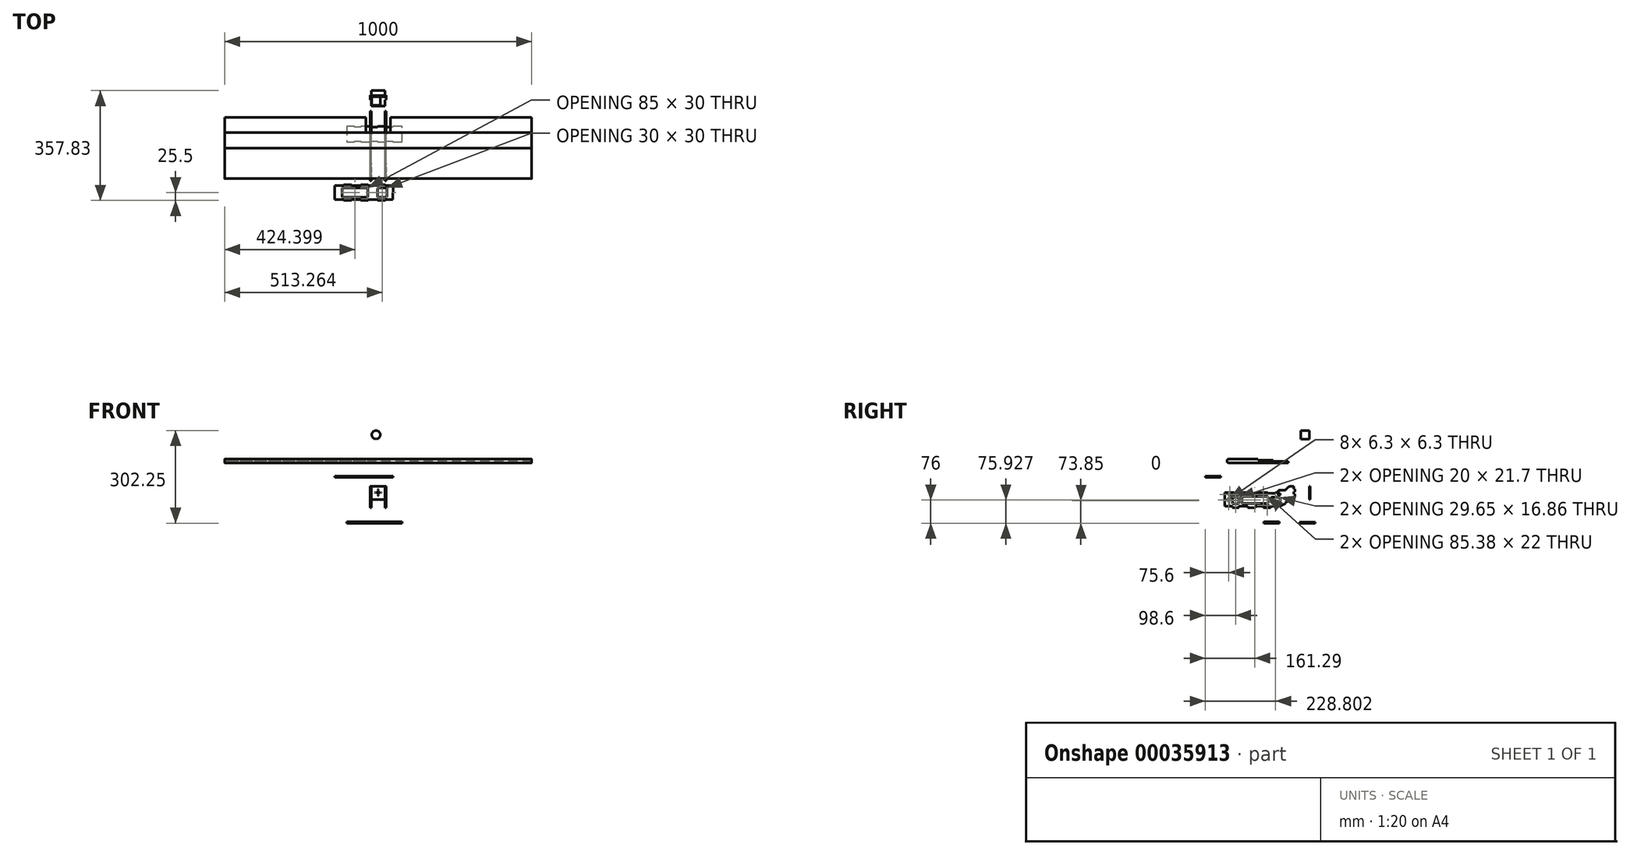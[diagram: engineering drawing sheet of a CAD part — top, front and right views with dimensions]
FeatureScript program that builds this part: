
annotation { "Feature Type Name" : "Feature", "Feature Type Description" : "" }
export const myFeature = defineFeature(function(context is Context, id is Id, definition is map)
    precondition{}
    {
        {
            var Q0;
            Q0=qCreatedBy(makeId("Right.planeOp"),FACE);
            cPlane(context, id + "F0", {"entities" : qUnion([Q0]), "cplaneType" : CPlaneType.OFFSET, "offset" : 22.5 * mm, "width" : 152.4 * mm, "height" : 152.4 * mm});
        }
        {
            var Q0;
            Q0=qCreatedBy(id+"F0.planeOp",FACE);
            var sketch = newSketch(context, id + "F1", { "sketchPlane" : qUnion([Q0])});
            skLineSegment(sketch, "E0", {"start": v(-125, 0) * mm, "end": v(-95, 0) * mm});
            skLineSegment(sketch, "E1", {"start": v(-125, -45) * mm, "end": v(-125, 0) * mm});
            skLineSegment(sketch, "E2", {"start": v(-95, 0) * mm, "end": v(-95, -3) * mm});
            skLineSegment(sketch, "E3", {"start": v(-95, -3) * mm, "end": v(-70, -3) * mm});
            skLineSegment(sketch, "E4", {"start": v(-70, -3) * mm, "end": v(-70, 0) * mm});
            skLineSegment(sketch, "E5", {"start": v(-40, 0) * mm, "end": v(-40, -3) * mm});
            skLineSegment(sketch, "E6", {"start": v(-40, -3) * mm, "end": v(-15, -3) * mm});
            skLineSegment(sketch, "E7", {"start": v(-15, -3) * mm, "end": v(-15, 0) * mm});
            skLineSegment(sketch, "E8", {"start": v(15, 0) * mm, "end": v(15, -3) * mm});
            skLineSegment(sketch, "E9", {"start": v(15, -3) * mm, "end": v(40, -3) * mm});
            skLineSegment(sketch, "E10", {"start": v(40, -3) * mm, "end": v(40, 0) * mm});
            skLineSegment(sketch, "E11", {"start": v(-70, 0) * mm, "end": v(-40, 0) * mm});
            skLineSegment(sketch, "E12", {"start": v(103, 11.5) * mm, "end": v(103, 3) * mm});
            skLineSegment(sketch, "E13", {"start": v(100, -22.5) * mm, "end": v(100, -14) * mm});
            skLineSegment(sketch, "E14", {"start": v(100, -14) * mm, "end": v(103, -14) * mm});
            skLineSegment(sketch, "E15", {"start": v(103, -14) * mm, "end": v(103, -5.5) * mm});
            skLineSegment(sketch, "E16", {"start": v(-125, -45) * mm, "end": v(-100, -45) * mm});
            skLineSegment(sketch, "E17", {"start": v(-100, -49.7) * mm, "end": v(-100, -45) * mm});
            skLineSegment(sketch, "E18", {"start": v(-100, -49.7) * mm, "end": v(-80, -49.7) * mm});
            skLineSegment(sketch, "E19", {"start": v(-80, -45) * mm, "end": v(-80, -49.7) * mm});
            skLineSegment(sketch, "E20", {"start": v(-80, -45) * mm, "end": v(-50, -45) * mm});
            skLineSegment(sketch, "E21", {"start": v(-50, -49.7) * mm, "end": v(-50, -45) * mm});
            skLineSegment(sketch, "E22", {"start": v(-50, -49.7) * mm, "end": v(-25, -49.7) * mm});
            skLineSegment(sketch, "E23", {"start": v(-25, -45) * mm, "end": v(-25, -49.7) * mm});
            skLineSegment(sketch, "E24", {"start": v(-25, -45) * mm, "end": v(0, -45) * mm});
            skLineSegment(sketch, "E25", {"start": v(0, -49.7) * mm, "end": v(0, -45) * mm});
            skLineSegment(sketch, "E26", {"start": v(0, -49.7) * mm, "end": v(25, -49.7) * mm});
            skLineSegment(sketch, "E27", {"start": v(25, -45) * mm, "end": v(25, -49.7) * mm});
            skLineSegment(sketch, "E28", {"start": v(25, -45) * mm, "end": v(55, -45) * mm});
            skLineSegment(sketch, "E29", {"start": v(103, -5.5) * mm, "end": v(100, -5.5) * mm});
            skLineSegment(sketch, "E30", {"start": v(100, -5.5) * mm, "end": v(100, 3) * mm});
            skLineSegment(sketch, "E31", {"start": v(100, 3) * mm, "end": v(103, 3) * mm});
            skLineSegment(sketch, "E32", {"start": v(103, 11.5) * mm, "end": v(100, 11.5) * mm});
            skLineSegment(sketch, "E33", {"start": v(100, 11.5) * mm, "end": v(100, 20) * mm});
            skLineSegment(sketch, "E34", {"start": v(100, 20) * mm, "end": v(87.07, 20) * mm});
            skLineSegment(sketch, "E35", {"start": v(55, -45) * mm, "end": v(72.89, -36.06) * mm});
            skLineSegment(sketch, "E36", {"start": v(86.3, -29.35) * mm, "end": v(100, -22.5) * mm});
            skLineSegment(sketch, "E37", {"start": v(72.89, -36.06) * mm, "end": v(71.55, -33.37) * mm});
            skLineSegment(sketch, "E38", {"start": v(86.3, -29.35) * mm, "end": v(84.96, -26.66) * mm});
            skLineSegment(sketch, "E39", {"start": v(71.55, -33.37) * mm, "end": v(84.96, -26.66) * mm});
            skLineSegment(sketch, "E40.rect.bottom", {"start": v(-83, -15.3) * mm, "end": v(-97, -15.3) * mm});
            skLineSegment(sketch, "E40.rect.top", {"start": v(-83, -37) * mm, "end": v(-97, -37) * mm});
            skLineSegment(sketch, "E40.rect.left", {"start": v(-80, -18.3) * mm, "end": v(-80, -34) * mm});
            skLineSegment(sketch, "E40.rect.right", {"start": v(-100, -18.3) * mm, "end": v(-100, -34) * mm});
            skPoint(sketch, "E40.rect.middle.positionSnap0", {"position": v(-125, -22.5) * mm});
            skPoint(sketch, "E40.rect.centerSnap0", {"position": v(-125, -22.5) * mm});
            skLineSegment(sketch, "E41.rect.bottom", {"start": v(52.03, -32.5) * mm, "end": v(28.38, -32.5) * mm});
            skLineSegment(sketch, "E41.rect.top", {"start": v(52.03, -15.64) * mm, "end": v(28.38, -15.64) * mm});
            skLineSegment(sketch, "E41.rect.left", {"start": v(55.03, -29.5) * mm, "end": v(55.03, -18.64) * mm});
            skLineSegment(sketch, "E41.rect.right", {"start": v(25.38, -29.5) * mm, "end": v(25.38, -18.64) * mm});
            skPoint(sketch, "E41.rect.middle", {"position": v(40.2, -24.07) * mm});
            skPoint(sketch, "E42.visualSharp", {"position": v(-100, -15.3) * mm});
            skArc(sketch, "E42.filletArc", {"start": v(-97, -15.3) * mm, "mid": v(-99.12, -16.18) * mm, "end": v(-100, -18.3) * mm});
            skPoint(sketch, "E43.visualSharp", {"position": v(-100, -37) * mm});
            skArc(sketch, "E43.filletArc", {"start": v(-100, -34) * mm, "mid": v(-99.12, -36.12) * mm, "end": v(-97, -37) * mm});
            skPoint(sketch, "E44.visualSharp", {"position": v(-80, -37) * mm});
            skArc(sketch, "E44.filletArc", {"start": v(-83, -37) * mm, "mid": v(-80.88, -36.12) * mm, "end": v(-80, -34) * mm});
            skPoint(sketch, "E45.visualSharp", {"position": v(-80, -15.3) * mm});
            skArc(sketch, "E45.filletArc", {"start": v(-80, -18.3) * mm, "mid": v(-80.88, -16.18) * mm, "end": v(-83, -15.3) * mm});
            skPoint(sketch, "E46.visualSharp", {"position": v(25.38, -32.5) * mm});
            skArc(sketch, "E46.filletArc", {"start": v(25.38, -29.5) * mm, "mid": v(26.26, -31.62) * mm, "end": v(28.38, -32.5) * mm});
            skPoint(sketch, "E47.visualSharp", {"position": v(25.38, -15.64) * mm});
            skArc(sketch, "E47.filletArc", {"start": v(28.38, -15.64) * mm, "mid": v(26.26, -16.52) * mm, "end": v(25.38, -18.64) * mm});
            skPoint(sketch, "E48.visualSharp", {"position": v(55.03, -15.64) * mm});
            skArc(sketch, "E48.filletArc", {"start": v(55.03, -18.64) * mm, "mid": v(54.15, -16.52) * mm, "end": v(52.03, -15.64) * mm});
            skPoint(sketch, "E49.visualSharp", {"position": v(55.03, -32.5) * mm});
            skArc(sketch, "E49.filletArc", {"start": v(52.03, -32.5) * mm, "mid": v(54.15, -31.62) * mm, "end": v(55.03, -29.5) * mm});
            skLineSegment(sketch, "E50.bottom", {"start": v(-68, -13) * mm, "end": v(13.38, -13) * mm});
            skLineSegment(sketch, "E50.top", {"start": v(-68, -35) * mm, "end": v(13.38, -35) * mm});
            skLineSegment(sketch, "E50.left", {"start": v(-70, -15) * mm, "end": v(-70, -33) * mm});
            skLineSegment(sketch, "E50.right", {"start": v(15.38, -15) * mm, "end": v(15.38, -33) * mm});
            skPoint(sketch, "E51.visualSharp", {"position": v(-70, -13) * mm});
            skArc(sketch, "E51.filletArc", {"start": v(-68, -13) * mm, "mid": v(-69.41, -13.59) * mm, "end": v(-70, -15) * mm});
            skPoint(sketch, "E52.visualSharp", {"position": v(-70, -35) * mm});
            skArc(sketch, "E52.filletArc", {"start": v(-70, -33) * mm, "mid": v(-69.41, -34.41) * mm, "end": v(-68, -35) * mm});
            skPoint(sketch, "E53.visualSharp", {"position": v(15.38, -13) * mm});
            skArc(sketch, "E53.filletArc", {"start": v(15.38, -15) * mm, "mid": v(14.8, -13.59) * mm, "end": v(13.38, -13) * mm});
            skPoint(sketch, "E54.visualSharp", {"position": v(15.38, -35) * mm});
            skArc(sketch, "E54.filletArc", {"start": v(13.38, -35) * mm, "mid": v(14.8, -34.41) * mm, "end": v(15.38, -33) * mm});
            skLineSegment(sketch, "E55.bottom", {"start": v(48.5, -3) * mm, "end": v(54.85, -3) * mm});
            skLineSegment(sketch, "E55.right", {"start": v(54.85, -3) * mm, "end": v(54.85, -9.35) * mm});
            skLineSegment(sketch, "E55.top", {"start": v(48.5, -9.35) * mm, "end": v(54.85, -9.35) * mm});
            skLineSegment(sketch, "E55.left", {"start": v(48.5, -3) * mm, "end": v(48.5, -9.35) * mm});
            skLineSegment(sketch, "E56.bottom", {"start": v(9.66, -38.7) * mm, "end": v(15.96, -38.7) * mm});
            skLineSegment(sketch, "E56.top", {"start": v(9.66, -45) * mm, "end": v(15.96, -45) * mm});
            skLineSegment(sketch, "E56.left", {"start": v(9.66, -38.7) * mm, "end": v(9.66, -45) * mm});
            skLineSegment(sketch, "E56.right", {"start": v(15.96, -38.7) * mm, "end": v(15.96, -45) * mm});
            skLineSegment(sketch, "E57.rect.bottom", {"start": v(-109.85, -20.85) * mm, "end": v(-116.15, -20.85) * mm});
            skLineSegment(sketch, "E57.rect.top", {"start": v(-109.85, -27.15) * mm, "end": v(-116.15, -27.15) * mm});
            skLineSegment(sketch, "E57.rect.left", {"start": v(-109.85, -20.85) * mm, "end": v(-109.85, -27.15) * mm});
            skLineSegment(sketch, "E57.rect.right", {"start": v(-116.15, -20.85) * mm, "end": v(-116.15, -27.15) * mm});
            skPoint(sketch, "E57.rect.middle", {"position": v(-113, -24) * mm});
            skLineSegment(sketch, "E58.rect.bottom", {"start": v(-105, -3) * mm, "end": v(-111.3, -3) * mm});
            skLineSegment(sketch, "E58.rect.top", {"start": v(-105, -9.3) * mm, "end": v(-111.3, -9.3) * mm});
            skLineSegment(sketch, "E58.rect.left", {"start": v(-105, -3) * mm, "end": v(-105, -9.3) * mm});
            skLineSegment(sketch, "E58.rect.right", {"start": v(-111.3, -3) * mm, "end": v(-111.3, -9.3) * mm});
            skPoint(sketch, "E58.rect.middle", {"position": v(-108.15, -6.15) * mm});
            skLineSegment(sketch, "E59", {"start": v(-15, 0) * mm, "end": v(15, 0) * mm});
            skLineSegment(sketch, "E60.bottom", {"start": v(-3.15, -3) * mm, "end": v(3.15, -3) * mm});
            skLineSegment(sketch, "E60.top", {"start": v(-3.15, -9.3) * mm, "end": v(3.15, -9.3) * mm});
            skLineSegment(sketch, "E60.left", {"start": v(-3.15, -3) * mm, "end": v(-3.15, -9.3) * mm});
            skLineSegment(sketch, "E60.right", {"start": v(3.15, -3) * mm, "end": v(3.15, -9.3) * mm});
            skLineSegment(sketch, "E61", {"start": v(48.5, 0) * mm, "end": v(40, 0) * mm});
            skLineSegment(sketch, "E62", {"start": v(48.5, 0) * mm, "end": v(48.5, 4) * mm});
            skLineSegment(sketch, "E63", {"start": v(51.5, 7) * mm, "end": v(69.93, 7) * mm});
            skLineSegment(sketch, "E64", {"start": v(83.54, 18.54) * mm, "end": v(73.46, 8.46) * mm});
            skPoint(sketch, "E65.visualSharp", {"position": v(85, 20) * mm});
            skArc(sketch, "E65.filletArc", {"start": v(87.07, 20) * mm, "mid": v(85.16, 19.62) * mm, "end": v(83.54, 18.54) * mm});
            skPoint(sketch, "E66.visualSharp", {"position": v(72, 7) * mm});
            skArc(sketch, "E66.filletArc", {"start": v(69.93, 7) * mm, "mid": v(71.84, 7.38) * mm, "end": v(73.46, 8.46) * mm});
            skPoint(sketch, "E67.visualSharp", {"position": v(48.5, 7) * mm});
            skArc(sketch, "E67.filletArc", {"start": v(51.5, 7) * mm, "mid": v(49.38, 6.12) * mm, "end": v(48.5, 4) * mm});
            skSolve(sketch);
        }
        {
            var Q0;
            Q0=makeQuery(id+"F1.imprint","IMPRINT",FACE,{"disambiguationData":[TD([[makeQuery(id+"F1.imprint","IMPRINT",EDGE,{"derivedFrom":sQuery(id+"F1.wireOp",EDGE,"E0")}),-1.0]])]});
            extrude(context, id + "F2", {"entities" : qUnion([Q0]), "depth" : 3 * mm});
        }
        {
            var Q0;
            Q0=makeQuery(id+"F2.opExtrude","SWEPT_BODY",BODY,{"disambiguationData":[OSD([sQuery(id+"F1.wireOp",EDGE,"E0"),sQuery(id+"F1.wireOp",EDGE,"8ebbecb4-de44-4d93-a758-2f3a406cd85b"),sQuery(id+"F1.wireOp",EDGE,"E1"),sQuery(id+"F1.wireOp",EDGE,"E2"),sQuery(id+"F1.wireOp",EDGE,"E3"),sQuery(id+"F1.wireOp",EDGE,"E4"),sQuery(id+"F1.wireOp",EDGE,"E5"),sQuery(id+"F1.wireOp",EDGE,"E6"),sQuery(id+"F1.wireOp",EDGE,"E7"),sQuery(id+"F1.wireOp",EDGE,"E8"),sQuery(id+"F1.wireOp",EDGE,"E9"),sQuery(id+"F1.wireOp",EDGE,"E10"),sQuery(id+"F1.wireOp",EDGE,"e3c22bda-0440-49f4-9c6e-7cd8685923fd"),sQuery(id+"F1.wireOp",EDGE,"E11"),sQuery(id+"F1.wireOp",EDGE,"E12"),sQuery(id+"F1.wireOp",EDGE,"E13"),sQuery(id+"F1.wireOp",EDGE,"E14"),sQuery(id+"F1.wireOp",EDGE,"E15"),sQuery(id+"F1.wireOp",EDGE,"E16"),sQuery(id+"F1.wireOp",EDGE,"E17"),sQuery(id+"F1.wireOp",EDGE,"E18"),sQuery(id+"F1.wireOp",EDGE,"E19"),sQuery(id+"F1.wireOp",EDGE,"E20"),sQuery(id+"F1.wireOp",EDGE,"E21"),sQuery(id+"F1.wireOp",EDGE,"E22"),sQuery(id+"F1.wireOp",EDGE,"E23"),sQuery(id+"F1.wireOp",EDGE,"E24"),sQuery(id+"F1.wireOp",EDGE,"E25"),sQuery(id+"F1.wireOp",EDGE,"E26"),sQuery(id+"F1.wireOp",EDGE,"E27"),sQuery(id+"F1.wireOp",EDGE,"E28"),sQuery(id+"F1.wireOp",EDGE,"E29"),sQuery(id+"F1.wireOp",EDGE,"E30"),sQuery(id+"F1.wireOp",EDGE,"E31"),sQuery(id+"F1.wireOp",EDGE,"E32"),sQuery(id+"F1.wireOp",EDGE,"E33"),sQuery(id+"F1.wireOp",EDGE,"E34"),sQuery(id+"F1.wireOp",EDGE,"825a1ea0-f497-42c9-b3a3-8482550d0f51"),sQuery(id+"F1.wireOp",EDGE,"6c7e5e58-49ee-4adc-a180-5d31e7a2f5a1")])]});
            var Q1;
            Q1=qCreatedBy(makeId("Right.planeOp"),FACE);
            mirror(context, id + "F3", {"entities" : qUnion([Q0]), "mirrorPlane" : qUnion([Q1])});
        }
        {
            var Q0;
            Q0=qCreatedBy(makeId("Front.planeOp"),FACE);
            cPlane(context, id + "F4", {"entities" : qUnion([Q0]), "cplaneType" : CPlaneType.OFFSET, "offset" : 150 * mm, "oppositeDirection" : true, "width" : 150 * mm, "height" : 150 * mm});
        }
        {
            var Q0;
            Q0=qCreatedBy(id+"F4.planeOp",FACE);
            var sketch = newSketch(context, id + "F5", { "sketchPlane" : qUnion([Q0])});
            skLineSegment(sketch, "E68", {"start": v(0, 20.05) * mm, "end": v(25.5, 20.05) * mm});
            skLineSegment(sketch, "E69", {"start": v(25.5, -22.45) * mm, "end": v(0, -22.45) * mm});
            skLineSegment(sketch, "E70", {"start": v(25.5, 20.05) * mm, "end": v(25.5, 11.55) * mm});
            skLineSegment(sketch, "E71", {"start": v(25.5, 11.55) * mm, "end": v(22.5, 11.55) * mm});
            skLineSegment(sketch, "E72", {"start": v(22.5, 11.55) * mm, "end": v(22.5, 3.05) * mm});
            skLineSegment(sketch, "E73", {"start": v(22.5, 3.05) * mm, "end": v(25.5, 3.05) * mm});
            skLineSegment(sketch, "E74", {"start": v(25.5, 3.05) * mm, "end": v(25.5, -5.45) * mm});
            skLineSegment(sketch, "E75", {"start": v(25.5, -5.45) * mm, "end": v(22.5, -5.45) * mm});
            skLineSegment(sketch, "E76", {"start": v(22.5, -5.45) * mm, "end": v(22.5, -13.95) * mm});
            skLineSegment(sketch, "E77", {"start": v(22.5, -13.95) * mm, "end": v(25.5, -13.95) * mm});
            skLineSegment(sketch, "E78", {"start": v(25.5, -13.95) * mm, "end": v(25.5, -22.45) * mm});
            skLineSegment(sketch, "E79", {"start": v(0, 20.05) * mm, "end": v(-25.5, 20.05) * mm});
            skLineSegment(sketch, "E80", {"start": v(-25.5, 20.05) * mm, "end": v(-25.5, 11.55) * mm});
            skLineSegment(sketch, "E81", {"start": v(-25.5, 11.55) * mm, "end": v(-22.5, 11.55) * mm});
            skLineSegment(sketch, "E82", {"start": v(-22.5, 11.55) * mm, "end": v(-22.5, 3.05) * mm});
            skLineSegment(sketch, "E83", {"start": v(-22.5, 3.05) * mm, "end": v(-25.5, 3.05) * mm});
            skLineSegment(sketch, "E84", {"start": v(-25.5, 3.05) * mm, "end": v(-25.5, -5.45) * mm});
            skLineSegment(sketch, "E85", {"start": v(-25.5, -5.45) * mm, "end": v(-22.5, -5.45) * mm});
            skLineSegment(sketch, "E86", {"start": v(-22.5, -5.45) * mm, "end": v(-22.5, -13.95) * mm});
            skLineSegment(sketch, "E87", {"start": v(-22.5, -13.95) * mm, "end": v(-25.5, -13.95) * mm});
            skLineSegment(sketch, "E88", {"start": v(-25.5, -13.95) * mm, "end": v(-25.5, -22.45) * mm});
            skLineSegment(sketch, "E89", {"start": v(-25.5, -22.45) * mm, "end": v(0, -22.45) * mm});
            skPoint(sketch, "E90", {"position": v(0, 9.5) * mm});
            skPoint(sketch, "E91", {"position": v(0, -9.5) * mm});
            skPoint(sketch, "E92", {"position": v(-9.5, 0) * mm});
            skPoint(sketch, "E93", {"position": v(9.5, 0) * mm});
            skCircle(sketch, "E94", {"center": v(0, 9.5) * mm, "radius": 0.5 * mm});
            skCircle(sketch, "E95", {"center": v(-9.5, 0) * mm, "radius": 0.5 * mm});
            skCircle(sketch, "E96", {"center": v(0, -9.5) * mm, "radius": 0.5 * mm});
            skCircle(sketch, "E97", {"center": v(9.5, 0) * mm, "radius": 0.5 * mm});
            skCircle(sketch, "E98", {"center": v(0, 0) * mm, "radius": 4 * mm});
            skSolve(sketch);
        }
        {
            var Q0;
            Q0 = qSketchRegion(id + "F5", true);
            extrude(context, id + "F6", {"entities" : qUnion([Q0]), "oppositeDirection" : true, "depth" : 3 * mm});
        }
        {
            var Q0;
            Q0=qCreatedBy(makeId("Top.planeOp"),FACE);
            cPlane(context, id + "F7", {"entities" : qUnion([Q0]), "cplaneType" : CPlaneType.OFFSET, "offset" : 50 * mm, "width" : 150 * mm, "height" : 150 * mm});
        }
        {
            var Q0;
            Q0=qCreatedBy(id+"F7.planeOp",FACE);
            var sketch = newSketch(context, id + "F8", { "sketchPlane" : qUnion([Q0])});
            skLineSegment(sketch, "E99", {"start": v(-97.13, -140.6) * mm, "end": v(-97.13, -110.6) * mm});
            skLineSegment(sketch, "E100", {"start": v(-94.13, -110.6) * mm, "end": v(-97.13, -110.6) * mm});
            skLineSegment(sketch, "E101", {"start": v(-94.13, -110.6) * mm, "end": v(-94.13, -85.6) * mm});
            skLineSegment(sketch, "E102", {"start": v(-97.13, -85.6) * mm, "end": v(-94.13, -85.6) * mm});
            skLineSegment(sketch, "E103", {"start": v(-97.13, -85.6) * mm, "end": v(-97.13, -55.6) * mm});
            skLineSegment(sketch, "E104", {"start": v(-94.13, -55.6) * mm, "end": v(-97.13, -55.6) * mm});
            skLineSegment(sketch, "E105", {"start": v(-94.13, -55.6) * mm, "end": v(-94.13, -30.6) * mm});
            skLineSegment(sketch, "E106", {"start": v(-97.13, -30.6) * mm, "end": v(-94.13, -30.6) * mm});
            skLineSegment(sketch, "E107", {"start": v(-97.13, -30.6) * mm, "end": v(-97.13, -0.6) * mm});
            skLineSegment(sketch, "E108", {"start": v(-94.13, -0.6) * mm, "end": v(-97.13, -0.6) * mm});
            skLineSegment(sketch, "E109", {"start": v(-94.13, -0.6) * mm, "end": v(-94.13, 24.4) * mm});
            skLineSegment(sketch, "E110", {"start": v(-97.13, 24.4) * mm, "end": v(-94.13, 24.4) * mm});
            skLineSegment(sketch, "E111", {"start": v(-97.13, 24.4) * mm, "end": v(-97.13, 49.4) * mm});
            skLineSegment(sketch, "E112", {"start": v(-142.13, 50.24) * mm, "end": v(-142.13, 24.4) * mm});
            skLineSegment(sketch, "E113", {"start": v(-145.13, 24.4) * mm, "end": v(-142.13, 24.4) * mm});
            skLineSegment(sketch, "E114", {"start": v(-145.13, 24.4) * mm, "end": v(-145.13, -0.6) * mm});
            skLineSegment(sketch, "E115", {"start": v(-142.13, -0.6) * mm, "end": v(-145.13, -0.6) * mm});
            skLineSegment(sketch, "E116", {"start": v(-142.13, -0.6) * mm, "end": v(-142.13, -30.6) * mm});
            skLineSegment(sketch, "E117", {"start": v(-145.13, -30.6) * mm, "end": v(-142.13, -30.6) * mm});
            skLineSegment(sketch, "E118", {"start": v(-145.13, -30.6) * mm, "end": v(-145.13, -55.6) * mm});
            skLineSegment(sketch, "E119", {"start": v(-142.13, -55.6) * mm, "end": v(-145.13, -55.6) * mm});
            skLineSegment(sketch, "E120", {"start": v(-142.13, -55.6) * mm, "end": v(-142.13, -85.6) * mm});
            skLineSegment(sketch, "E121", {"start": v(-145.13, -85.6) * mm, "end": v(-142.13, -85.6) * mm});
            skLineSegment(sketch, "E122", {"start": v(-145.13, -85.6) * mm, "end": v(-145.13, -110.6) * mm});
            skLineSegment(sketch, "E123", {"start": v(-142.13, -110.6) * mm, "end": v(-145.13, -110.6) * mm});
            skLineSegment(sketch, "E124", {"start": v(-142.13, -110.6) * mm, "end": v(-142.13, -140.6) * mm});
            skLineSegment(sketch, "E125", {"start": v(-97.13, -140.6) * mm, "end": v(-142.13, -140.6) * mm});
            skLineSegment(sketch, "E126", {"start": v(-97.13, 49.4) * mm, "end": v(-142.13, 50.24) * mm});
            skPoint(sketch, "E127.rect.middle.positionSnap0", {"position": v(-119.63, -140.6) * mm});
            skPoint(sketch, "E127.rect.centerSnap0", {"position": v(-119.63, -140.6) * mm});
            skPoint(sketch, "E128.rect.centerSnap0", {"position": v(-116.22, -35.83) * mm});
            skPoint(sketch, "E128.rect.middle.positionSnap0", {"position": v(-116.22, -35.83) * mm});
            skPoint(sketch, "E129.rect.middle.positionSnap0", {"position": v(-119.63, 49.82) * mm});
            skPoint(sketch, "E129.rect.centerSnap0", {"position": v(-119.63, 49.82) * mm});
            skLineSegment(sketch, "E130.rect.bottom", {"start": v(-131.63, -31.58) * mm, "end": v(-107.63, -31.58) * mm});
            skLineSegment(sketch, "E130.rect.top", {"start": v(-131.63, -116.58) * mm, "end": v(-107.63, -116.58) * mm});
            skLineSegment(sketch, "E130.rect.left", {"start": v(-134.63, -34.58) * mm, "end": v(-134.63, -113.58) * mm});
            skLineSegment(sketch, "E130.rect.right", {"start": v(-104.63, -34.58) * mm, "end": v(-104.63, -113.58) * mm});
            skPoint(sketch, "E130.rect.middle", {"position": v(-119.63, -74.08) * mm});
            skPoint(sketch, "E131.visualSharp", {"position": v(-134.63, -116.58) * mm});
            skArc(sketch, "E131.filletArc", {"start": v(-134.63, -113.58) * mm, "mid": v(-133.75, -115.7) * mm, "end": v(-131.63, -116.58) * mm});
            skPoint(sketch, "E132.visualSharp", {"position": v(-104.63, -116.58) * mm});
            skArc(sketch, "E132.filletArc", {"start": v(-107.63, -116.58) * mm, "mid": v(-105.5, -115.7) * mm, "end": v(-104.63, -113.58) * mm});
            skPoint(sketch, "E133.visualSharp", {"position": v(-134.63, -31.58) * mm});
            skArc(sketch, "E133.filletArc", {"start": v(-131.63, -31.58) * mm, "mid": v(-133.75, -32.45) * mm, "end": v(-134.63, -34.58) * mm});
            skPoint(sketch, "E134.visualSharp", {"position": v(-104.63, -31.58) * mm});
            skArc(sketch, "E134.filletArc", {"start": v(-104.63, -34.58) * mm, "mid": v(-105.5, -32.45) * mm, "end": v(-107.63, -31.58) * mm});
            skLineSegment(sketch, "E135.rect.bottom", {"start": v(-107.63, -0.2) * mm, "end": v(-131.63, -0.2) * mm});
            skLineSegment(sketch, "E135.rect.top", {"start": v(-107.63, 29.8) * mm, "end": v(-131.63, 29.8) * mm});
            skLineSegment(sketch, "E135.rect.left", {"start": v(-104.63, 2.8) * mm, "end": v(-104.63, 26.8) * mm});
            skLineSegment(sketch, "E135.rect.right", {"start": v(-134.63, 2.8) * mm, "end": v(-134.63, 26.8) * mm});
            skPoint(sketch, "E135.rect.middle", {"position": v(-119.63, 14.8) * mm});
            skPoint(sketch, "E136.visualSharp", {"position": v(-134.63, 29.8) * mm});
            skArc(sketch, "E136.filletArc", {"start": v(-131.63, 29.8) * mm, "mid": v(-133.75, 28.91) * mm, "end": v(-134.63, 26.8) * mm});
            skPoint(sketch, "E137.visualSharp", {"position": v(-104.63, 29.8) * mm});
            skArc(sketch, "E137.filletArc", {"start": v(-104.63, 26.8) * mm, "mid": v(-105.5, 28.91) * mm, "end": v(-107.63, 29.8) * mm});
            skPoint(sketch, "E138.visualSharp", {"position": v(-104.63, -0.2) * mm});
            skArc(sketch, "E138.filletArc", {"start": v(-107.63, -0.2) * mm, "mid": v(-105.5, 0.67) * mm, "end": v(-104.63, 2.8) * mm});
            skPoint(sketch, "E139.visualSharp", {"position": v(-134.63, -0.2) * mm});
            skArc(sketch, "E139.filletArc", {"start": v(-134.63, 2.8) * mm, "mid": v(-133.75, 0.67) * mm, "end": v(-131.63, -0.2) * mm});
            skSolve(sketch);
        }
        {
            var Q0;
            Q0 = qSketchRegion(id + "F8", true);
            extrude(context, id + "F9", {"entities" : qUnion([Q0]), "depth" : 3 * mm});
        }
        {
            var Q0;
            Q0=qCreatedBy(makeId("Top.planeOp"),FACE);
            cPlane(context, id + "F10", {"entities" : qUnion([Q0]), "cplaneType" : CPlaneType.OFFSET, "offset" : 100 * mm, "oppositeDirection" : true, "width" : 150 * mm, "height" : 150 * mm});
        }
        {
            var Q0;
            Q0=qCreatedBy(id+"F10.planeOp",FACE);
            var sketch = newSketch(context, id + "F11", { "sketchPlane" : qUnion([Q0])});
            skLineSegment(sketch, "E140", {"start": v(78.08, -177.86) * mm, "end": v(78.08, -152.86) * mm});
            skLineSegment(sketch, "E141", {"start": v(78.08, -152.86) * mm, "end": v(75.08, -152.86) * mm});
            skLineSegment(sketch, "E142", {"start": v(75.08, -152.86) * mm, "end": v(75.08, -132.86) * mm});
            skLineSegment(sketch, "E143", {"start": v(75.08, -132.86) * mm, "end": v(78.08, -132.86) * mm});
            skLineSegment(sketch, "E144", {"start": v(78.08, -132.86) * mm, "end": v(78.08, -102.86) * mm});
            skLineSegment(sketch, "E145", {"start": v(78.08, -102.86) * mm, "end": v(75.08, -102.86) * mm});
            skLineSegment(sketch, "E146", {"start": v(75.08, -102.86) * mm, "end": v(75.08, -77.86) * mm});
            skLineSegment(sketch, "E147", {"start": v(75.08, -77.86) * mm, "end": v(78.08, -77.86) * mm});
            skLineSegment(sketch, "E148", {"start": v(78.08, -77.86) * mm, "end": v(78.08, -52.86) * mm});
            skLineSegment(sketch, "E149", {"start": v(78.08, -52.86) * mm, "end": v(75.08, -52.86) * mm});
            skLineSegment(sketch, "E150", {"start": v(75.08, -52.86) * mm, "end": v(75.08, -27.86) * mm});
            skLineSegment(sketch, "E151", {"start": v(75.08, -27.86) * mm, "end": v(78.08, -27.86) * mm});
            skLineSegment(sketch, "E152", {"start": v(78.08, -27.86) * mm, "end": v(78.08, 2.14) * mm});
            skLineSegment(sketch, "E153", {"start": v(78.08, 2.14) * mm, "end": v(27.08, 2.14) * mm});
            skLineSegment(sketch, "E154", {"start": v(27.08, 2.14) * mm, "end": v(27.08, -27.86) * mm});
            skLineSegment(sketch, "E155", {"start": v(27.08, -27.86) * mm, "end": v(30.08, -27.86) * mm});
            skLineSegment(sketch, "E156", {"start": v(30.08, -27.86) * mm, "end": v(30.08, -52.86) * mm});
            skLineSegment(sketch, "E157", {"start": v(30.08, -52.86) * mm, "end": v(27.08, -52.86) * mm});
            skLineSegment(sketch, "E158", {"start": v(27.08, -52.86) * mm, "end": v(27.08, -77.86) * mm});
            skLineSegment(sketch, "E159", {"start": v(27.08, -77.86) * mm, "end": v(30.08, -77.86) * mm});
            skLineSegment(sketch, "E160", {"start": v(30.08, -77.86) * mm, "end": v(30.08, -102.86) * mm});
            skLineSegment(sketch, "E161", {"start": v(30.08, -102.86) * mm, "end": v(27.08, -102.86) * mm});
            skLineSegment(sketch, "E162", {"start": v(27.08, -102.86) * mm, "end": v(27.08, -132.86) * mm});
            skLineSegment(sketch, "E163", {"start": v(27.08, -132.86) * mm, "end": v(30.08, -132.86) * mm});
            skLineSegment(sketch, "E164", {"start": v(30.08, -132.86) * mm, "end": v(30.08, -152.86) * mm});
            skLineSegment(sketch, "E165", {"start": v(30.08, -152.86) * mm, "end": v(27.08, -152.86) * mm});
            skLineSegment(sketch, "E166", {"start": v(27.08, -152.86) * mm, "end": v(27.08, -177.86) * mm});
            skLineSegment(sketch, "E167", {"start": v(27.08, -177.86) * mm, "end": v(78.08, -177.86) * mm});
            skSolve(sketch);
        }
        {
            var Q0;
            Q0 = qSketchRegion(id + "F11", true);
            extrude(context, id + "F12", {"entities" : qUnion([Q0]), "depth" : 4.7 * mm});
        }
        {
            var Q0;
            Q0=qCreatedBy(id+"F10.planeOp",FACE);
            var sketch = newSketch(context, id + "F13", { "sketchPlane" : qUnion([Q0])});
            skLineSegment(sketch, "E168.rect.bottom", {"start": v(-22.5, 169.23) * mm, "end": v(22.5, 169.23) * mm});
            skLineSegment(sketch, "E168.rect.top", {"start": v(-22.5, 119.23) * mm, "end": v(22.5, 119.23) * mm});
            skPoint(sketch, "E168.rect.middle", {"position": v(0, 144.23) * mm});
            skLineSegment(sketch, "E169", {"start": v(-22.5, 119.23) * mm, "end": v(-22.5, 139.23) * mm});
            skLineSegment(sketch, "E170", {"start": v(-22.5, 139.23) * mm, "end": v(-25.5, 139.23) * mm});
            skLineSegment(sketch, "E171", {"start": v(-25.5, 139.23) * mm, "end": v(-25.5, 154.23) * mm});
            skLineSegment(sketch, "E172", {"start": v(-25.5, 154.23) * mm, "end": v(-22.5, 154.23) * mm});
            skLineSegment(sketch, "E173", {"start": v(-22.5, 154.23) * mm, "end": v(-22.5, 169.23) * mm});
            skLineSegment(sketch, "E174", {"start": v(22.5, 119.23) * mm, "end": v(22.5, 139.23) * mm});
            skLineSegment(sketch, "E175", {"start": v(22.5, 139.23) * mm, "end": v(25.5, 139.23) * mm});
            skLineSegment(sketch, "E176", {"start": v(25.5, 139.23) * mm, "end": v(25.5, 154.23) * mm});
            skLineSegment(sketch, "E177", {"start": v(25.5, 154.23) * mm, "end": v(22.5, 154.23) * mm});
            skLineSegment(sketch, "E178", {"start": v(22.5, 154.23) * mm, "end": v(22.5, 169.23) * mm});
            skSolve(sketch);
        }
        {
            var Q0;
            Q0 = qSketchRegion(id + "F13", true);
            extrude(context, id + "F14", {"entities" : qUnion([Q0]), "depth" : 3 * mm});
        }
        {
            var Q0;
            Q0=makeQuery(id+"F9.opExtrude","SWEPT_BODY",BODY,{"disambiguationData":[OSD([sQuery(id+"F8.wireOp",EDGE,"E99"),sQuery(id+"F8.wireOp",EDGE,"E100"),sQuery(id+"F8.wireOp",EDGE,"E101"),sQuery(id+"F8.wireOp",EDGE,"E102"),sQuery(id+"F8.wireOp",EDGE,"E103"),sQuery(id+"F8.wireOp",EDGE,"E104"),sQuery(id+"F8.wireOp",EDGE,"E105"),sQuery(id+"F8.wireOp",EDGE,"E106"),sQuery(id+"F8.wireOp",EDGE,"E107"),sQuery(id+"F8.wireOp",EDGE,"E108"),sQuery(id+"F8.wireOp",EDGE,"E109"),sQuery(id+"F8.wireOp",EDGE,"E110"),sQuery(id+"F8.wireOp",EDGE,"E111"),sQuery(id+"F8.wireOp",EDGE,"E112"),sQuery(id+"F8.wireOp",EDGE,"E113"),sQuery(id+"F8.wireOp",EDGE,"E114"),sQuery(id+"F8.wireOp",EDGE,"E115"),sQuery(id+"F8.wireOp",EDGE,"E116"),sQuery(id+"F8.wireOp",EDGE,"E117"),sQuery(id+"F8.wireOp",EDGE,"E118"),sQuery(id+"F8.wireOp",EDGE,"E119"),sQuery(id+"F8.wireOp",EDGE,"E120"),sQuery(id+"F8.wireOp",EDGE,"E121"),sQuery(id+"F8.wireOp",EDGE,"E122"),sQuery(id+"F8.wireOp",EDGE,"E123"),sQuery(id+"F8.wireOp",EDGE,"E124"),sQuery(id+"F8.wireOp",EDGE,"E125"),sQuery(id+"F8.wireOp",EDGE,"E126"),sQuery(id+"F8.wireOp",EDGE,"f7f54e45-e327-43dd-8dbd-0f3e16c89ed2.rect.top"),sQuery(id+"F8.wireOp",EDGE,"f7f54e45-e327-43dd-8dbd-0f3e16c89ed2.rect.left"),sQuery(id+"F8.wireOp",EDGE,"d3c95a23-e058-4216-adf1-87267c1826a6"),sQuery(id+"F8.wireOp",EDGE,"c21961cd-536b-4800-8952-ef4d4e378895.filletArc"),sQuery(id+"F8.wireOp",EDGE,"e840e9a9-50be-48b6-bce8-9dc900ce0ec8.filletArc"),sQuery(id+"F8.wireOp",EDGE,"f739e3e5-072a-4ce8-8155-8baccca66ec6.filletArc"),sQuery(id+"F8.wireOp",EDGE,"50cf0aec-5b26-4f39-bb3c-843bb3447083.rect.bottom"),sQuery(id+"F8.wireOp",EDGE,"50cf0aec-5b26-4f39-bb3c-843bb3447083.rect.right"),sQuery(id+"F8.wireOp",EDGE,"b3e4471d-413f-4539-9826-dae95c2aa1e4"),sQuery(id+"F8.wireOp",EDGE,"32a9ddc1-724e-4596-9dee-e69c451e43e7.filletArc"),sQuery(id+"F8.wireOp",EDGE,"e3aaa05e-d2f8-4f91-bffd-5c4eec12b8fb.filletArc"),sQuery(id+"F8.wireOp",EDGE,"40547577-a187-47be-ab89-db573b5d3bc6.filletArc"),sQuery(id+"F8.wireOp",EDGE,"b4e90f19-44ae-4a60-acba-eca1facfac92"),sQuery(id+"F8.wireOp",EDGE,"4d5210fd-1cd2-4a8c-aa1f-1477e534c2fe.rect.bottom"),sQuery(id+"F8.wireOp",EDGE,"4d5210fd-1cd2-4a8c-aa1f-1477e534c2fe.rect.right"),sQuery(id+"F8.wireOp",EDGE,"2aa71f17-a767-4b0d-bfb4-584af78135c1"),sQuery(id+"F8.wireOp",EDGE,"b0c97619-6cc2-4a42-8839-dacbd89b7338.rect.left"),sQuery(id+"F8.wireOp",EDGE,"b0c97619-6cc2-4a42-8839-dacbd89b7338.rect.top"),sQuery(id+"F8.wireOp",EDGE,"dc025666-00a8-457b-8b33-3ff0116518ca.filletArc"),sQuery(id+"F8.wireOp",EDGE,"0ea78164-e0f1-4ca5-bbb2-ddf5f5a8cea7.filletArc"),sQuery(id+"F8.wireOp",EDGE,"90e7d81c-150c-4039-8b2b-79f28a453a8e.filletArc"),sQuery(id+"F8.wireOp",EDGE,"9a78d857-b6a5-4370-af2c-201379c90102.filletArc"),sQuery(id+"F8.wireOp",EDGE,"83f7d843-6f50-46a6-9c51-1e62a47ef275.filletArc"),sQuery(id+"F8.wireOp",EDGE,"b3f657bb-8713-434e-a4ac-e9452316884e.filletArc"),sQuery(id+"F8.wireOp",EDGE,"E129.rect.bottom"),sQuery(id+"F8.wireOp",EDGE,"E129.rect.top"),sQuery(id+"F8.wireOp",EDGE,"E129.rect.left"),sQuery(id+"F8.wireOp",EDGE,"E129.rect.right"),sQuery(id+"F8.wireOp",EDGE,"80fef93d-cb2b-4a93-81d4-590429a25baf.filletArc"),sQuery(id+"F8.wireOp",EDGE,"b041f558-92e8-420c-bcc1-398c1bb6d8a6.filletArc"),sQuery(id+"F8.wireOp",EDGE,"658f6547-300f-422c-b35b-7a56ffd5d901.filletArc"),sQuery(id+"F8.wireOp",EDGE,"24cd2aa6-13b3-4fbc-83dc-db5abd7e49f5.filletArc")])]});
            var Q1;
            Q1=makeQuery(id+"F9.opExtrude","SWEPT_EDGE",EDGE,{"disambiguationData":[OSD([sQuery(id+"F8.wireOp",EDGE,"E124"),sQuery(id+"F8.wireOp",EDGE,"E125")])]});
            transform(context, id + "F15", {"entities" : qUnion([Q0]), "transformType" : TransformType.ROTATION, "transformAxis" : qUnion([Q1]), "angle" : 90 * degree, "makeCopy" : false});
        }
        {
            var Q0;
            Q0=makeQuery(id+"F12.opExtrude","SWEPT_BODY",BODY,{"disambiguationData":[OSD([sQuery(id+"F11.wireOp",EDGE,"E140"),sQuery(id+"F11.wireOp",EDGE,"E141"),sQuery(id+"F11.wireOp",EDGE,"E142"),sQuery(id+"F11.wireOp",EDGE,"E143"),sQuery(id+"F11.wireOp",EDGE,"E144"),sQuery(id+"F11.wireOp",EDGE,"E145"),sQuery(id+"F11.wireOp",EDGE,"E146"),sQuery(id+"F11.wireOp",EDGE,"E147"),sQuery(id+"F11.wireOp",EDGE,"E148"),sQuery(id+"F11.wireOp",EDGE,"E149"),sQuery(id+"F11.wireOp",EDGE,"E150"),sQuery(id+"F11.wireOp",EDGE,"E151"),sQuery(id+"F11.wireOp",EDGE,"E152"),sQuery(id+"F11.wireOp",EDGE,"E153"),sQuery(id+"F11.wireOp",EDGE,"E154"),sQuery(id+"F11.wireOp",EDGE,"E155"),sQuery(id+"F11.wireOp",EDGE,"E156"),sQuery(id+"F11.wireOp",EDGE,"E157"),sQuery(id+"F11.wireOp",EDGE,"E158"),sQuery(id+"F11.wireOp",EDGE,"E159"),sQuery(id+"F11.wireOp",EDGE,"E160"),sQuery(id+"F11.wireOp",EDGE,"E161"),sQuery(id+"F11.wireOp",EDGE,"E162"),sQuery(id+"F11.wireOp",EDGE,"E163"),sQuery(id+"F11.wireOp",EDGE,"E164"),sQuery(id+"F11.wireOp",EDGE,"E165"),sQuery(id+"F11.wireOp",EDGE,"E166"),sQuery(id+"F11.wireOp",EDGE,"E167")])]});
            var Q1;
            Q1=makeQuery(id+"F12.opExtrude","SWEPT_EDGE",EDGE,{"disambiguationData":[OSD([sQuery(id+"F11.wireOp",EDGE,"E152"),sQuery(id+"F11.wireOp",EDGE,"E153")])]});
            transform(context, id + "F16", {"entities" : qUnion([Q0]), "transformType" : TransformType.ROTATION, "transformAxis" : qUnion([Q1]), "angle" : 90 * degree, "makeCopy" : false});
        }
        {
            var Q0;
            Q0=qCreatedBy(makeId("Right.planeOp"),FACE);
            var sketch = newSketch(context, id + "F17", { "sketchPlane" : qUnion([Q0])});
            skLineSegment(sketch, "E179", {"start": v(-117.9, 103.95) * mm, "end": v(-117.9, 101.95) * mm});
            skLineSegment(sketch, "E180", {"start": v(-112.9, 96.95) * mm, "end": v(82.1, 96.95) * mm});
            skLineSegment(sketch, "E181", {"start": v(82.1, 96.95) * mm, "end": v(82.1, 100.95) * mm});
            skLineSegment(sketch, "E182", {"start": v(82.1, 100.95) * mm, "end": v(32.1, 100.95) * mm});
            skLineSegment(sketch, "E183", {"start": v(32.1, 100.95) * mm, "end": v(32.1, 104.95) * mm});
            skLineSegment(sketch, "E184", {"start": v(32.1, 104.95) * mm, "end": v(-17.9, 104.95) * mm});
            skLineSegment(sketch, "E185", {"start": v(-17.9, 104.95) * mm, "end": v(-17.9, 108.95) * mm});
            skLineSegment(sketch, "E186", {"start": v(-17.9, 108.95) * mm, "end": v(-112.9, 108.95) * mm});
            skPoint(sketch, "E187.visualSharp", {"position": v(-117.9, 108.95) * mm});
            skArc(sketch, "E187.filletArc", {"start": v(-112.9, 108.95) * mm, "mid": v(-116.43, 107.48) * mm, "end": v(-117.9, 103.95) * mm});
            skPoint(sketch, "E188.visualSharp", {"position": v(-117.9, 96.95) * mm});
            skArc(sketch, "E188.filletArc", {"start": v(-117.9, 101.95) * mm, "mid": v(-116.43, 98.41) * mm, "end": v(-112.9, 96.95) * mm});
            skSolve(sketch);
        }
        {
            var Q0;
            Q0 = qSketchRegion(id + "F17", true);
            extrude(context, id + "F18", {"entities" : qUnion([Q0]), "endBound" : BoundingType.SYMMETRIC, "depth" : 1000 * mm});
        }
        {
            var Q0;
            Q0=qCreatedBy(makeId("Right.planeOp"),FACE);
            var sketch = newSketch(context, id + "F19", { "sketchPlane" : qUnion([Q0])});
            skLineSegment(sketch, "E189.rect.bottom", {"start": v(51.92, 40.02) * mm, "end": v(1.92, 40.02) * mm});
            skLineSegment(sketch, "E189.rect.top", {"start": v(51.92, 85.26) * mm, "end": v(1.92, 85.26) * mm});
            skLineSegment(sketch, "E189.rect.left", {"start": v(51.92, 40.02) * mm, "end": v(51.92, 85.26) * mm});
            skLineSegment(sketch, "E189.rect.right", {"start": v(1.92, 40.02) * mm, "end": v(1.92, 85.26) * mm});
            skPoint(sketch, "E189.rect.middle", {"position": v(26.92, 62.64) * mm});
            skSolve(sketch);
        }
        {
            var Q0;
            Q0 = qSketchRegion(id + "F19", true);
            extrude(context, id + "F20", {"entities" : qUnion([Q0]), "endBound" : BoundingType.SYMMETRIC, "depth" : 80 * mm});
        }
        {
            var Q0;
            Q0=makeQuery(id+"F20.opExtrude","SWEPT_BODY",BODY,{"disambiguationData":[OSD([sQuery(id+"F19.wireOp",EDGE,"E189.rect.bottom"),sQuery(id+"F19.wireOp",EDGE,"E189.rect.top"),sQuery(id+"F19.wireOp",EDGE,"E189.rect.left"),sQuery(id+"F19.wireOp",EDGE,"E189.rect.right")])]});
            transform(context, id + "F21", {"entities" : qUnion([Q0]), "transformType" : TransformType.TRANSLATION_3D, "dx" : 0 * mm, "dy" : 30.42 * mm, "dz" : 35.26 * mm, "makeCopy" : false});
        }
        {
            var Q0;
            Q0=makeQuery(id+"F20.opExtrude","SWEPT_BODY",BODY,{"disambiguationData":[OSD([sQuery(id+"F19.wireOp",EDGE,"E189.rect.bottom"),sQuery(id+"F19.wireOp",EDGE,"E189.rect.top"),sQuery(id+"F19.wireOp",EDGE,"E189.rect.left"),sQuery(id+"F19.wireOp",EDGE,"E189.rect.right")])]});
            var Q1;
            Q1=makeQuery(id+"F18.opExtrude","SWEPT_BODY",BODY,{"disambiguationData":[OSD([sQuery(id+"F17.wireOp",EDGE,"E179"),sQuery(id+"F17.wireOp",EDGE,"E180"),sQuery(id+"F17.wireOp",EDGE,"E181"),sQuery(id+"F17.wireOp",EDGE,"E182"),sQuery(id+"F17.wireOp",EDGE,"E183"),sQuery(id+"F17.wireOp",EDGE,"E184"),sQuery(id+"F17.wireOp",EDGE,"E185"),sQuery(id+"F17.wireOp",EDGE,"E186"),sQuery(id+"F17.wireOp",EDGE,"E187.filletArc"),sQuery(id+"F17.wireOp",EDGE,"E188.filletArc")])]});
            booleanBodies(context, id + "F22", {"operationType" : BooleanOperationType.SUBTRACTION, "tools" : qUnion([Q0]), "targets" : qUnion([Q1])});
        }
        {
            var Q0;
            Q0=qCreatedBy(makeId("Right.planeOp"),FACE);
            cPlane(context, id + "F23", {"entities" : qUnion([Q0]), "cplaneType" : CPlaneType.OFFSET, "offset" : 20 * mm, "oppositeDirection" : true, "width" : 150 * mm, "height" : 150 * mm});
        }
        {
            var Q0;
            Q0=qCreatedBy(id+"F4.planeOp",FACE);
            var sketch = newSketch(context, id + "F24", { "sketchPlane" : qUnion([Q0])});
            skCircle(sketch, "E190", {"center": v(-7.03, 188.4) * mm, "radius": 13.85 * mm});
            skSolve(sketch);
        }
        {
            var Q0;
            Q0=makeQuery(id+"F24.imprint","IMPRINT",FACE,{"disambiguationData":[TD([[makeQuery(id+"F24.imprint","IMPRINT",EDGE,{"derivedFrom":sQuery(id+"F24.wireOp",EDGE,"E190")}),1.0]])]});
            extrude(context, id + "F25", {"entities" : qUnion([Q0]), "depth" : 28 * mm});
        }
    });
